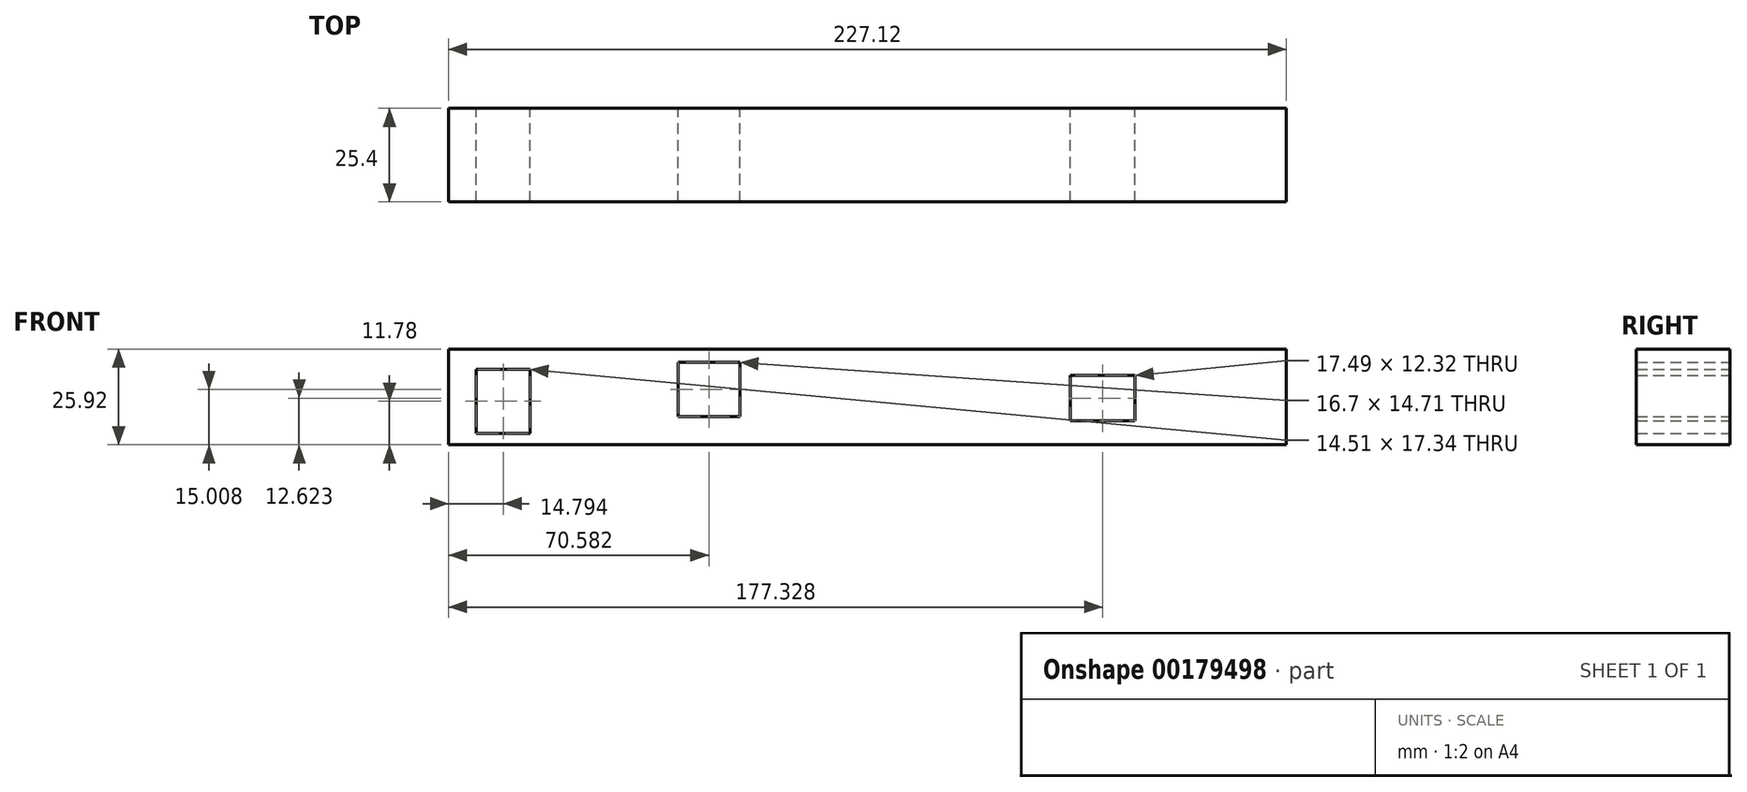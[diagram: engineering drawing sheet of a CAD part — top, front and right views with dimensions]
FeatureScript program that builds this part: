
annotation { "Feature Type Name" : "Feature", "Feature Type Description" : "" }
export const myFeature = defineFeature(function(context is Context, id is Id, definition is map)
    precondition{}
    {
        {
            var Q0;
            Q0=qCreatedBy(makeId("Front.planeOp"),FACE);
            var sketch = newSketch(context, id + "F0", { "sketchPlane" : qUnion([Q0])});
            skLineSegment(sketch, "E0.bottom", {"start": v(-72.94, 25.92) * mm, "end": v(154.18, 25.92) * mm});
            skLineSegment(sketch, "E0.top", {"start": v(-72.94, 0) * mm, "end": v(154.18, 0) * mm});
            skLineSegment(sketch, "E0.left", {"start": v(-72.94, 25.92) * mm, "end": v(-72.94, 0) * mm});
            skLineSegment(sketch, "E0.right", {"start": v(154.18, 25.92) * mm, "end": v(154.18, 0) * mm});
            skLineSegment(sketch, "E1.bottom", {"start": v(-65.4, 20.45) * mm, "end": v(-50.89, 20.45) * mm});
            skLineSegment(sketch, "E1.top", {"start": v(-65.4, 3.1) * mm, "end": v(-50.89, 3.1) * mm});
            skLineSegment(sketch, "E1.left", {"start": v(-65.4, 20.45) * mm, "end": v(-65.4, 3.1) * mm});
            skLineSegment(sketch, "E1.right", {"start": v(-50.89, 20.45) * mm, "end": v(-50.89, 3.1) * mm});
            skLineSegment(sketch, "E2.bottom", {"start": v(-10.7, 22.36) * mm, "end": v(6, 22.36) * mm});
            skLineSegment(sketch, "E2.top", {"start": v(-10.7, 7.65) * mm, "end": v(6, 7.65) * mm});
            skLineSegment(sketch, "E2.left", {"start": v(-10.7, 22.36) * mm, "end": v(-10.7, 7.65) * mm});
            skLineSegment(sketch, "E2.right", {"start": v(6, 22.36) * mm, "end": v(6, 7.65) * mm});
            skLineSegment(sketch, "E3.bottom", {"start": v(95.64, 18.78) * mm, "end": v(113.13, 18.78) * mm});
            skLineSegment(sketch, "E3.top", {"start": v(95.64, 6.46) * mm, "end": v(113.13, 6.46) * mm});
            skLineSegment(sketch, "E3.left", {"start": v(95.64, 18.78) * mm, "end": v(95.64, 6.46) * mm});
            skLineSegment(sketch, "E3.right", {"start": v(113.13, 18.78) * mm, "end": v(113.13, 6.46) * mm});
            skSolve(sketch);
        }
        {
            var Q0;
            Q0=makeQuery(id+"F0.imprint","IMPRINT",FACE,{"disambiguationData":[TD([[makeQuery(id+"F0.imprint","IMPRINT",EDGE,{"derivedFrom":sQuery(id+"F0.wireOp",EDGE,"E0.bottom")}),-1.0]])]});
            extrude(context, id + "F1", {"entities" : qUnion([Q0]), "depth" : 25.4 * mm});
        }
    });
